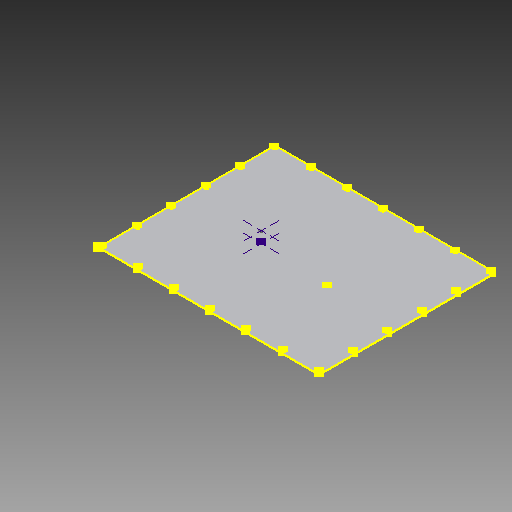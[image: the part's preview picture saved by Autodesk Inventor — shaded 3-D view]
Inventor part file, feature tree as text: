
AUTODESK INVENTOR PART (.ipt)
format: ipt  version: 2017 (Build 210142000, 142)  size: 188,416 bytes
history: native  units: in
note: dims shown in document units (in); Inventor stores cm internally (conversion verified against a paired STEP export)
features: sketch x5, hole x4, pattern_linear x4, extrude x1
ambient origin geometry x8: Origin, YZ Plane, XZ Plane, XY Plane, X Axis, Y Axis, Z Axis, Center Point
bodies: Solid1 (feature_tree)
feature tree (14):
  extrude  "Extrusion1"  Depth=8.0in
  sketch  "Sketch2"  dims[d4=0.06in d5=0.0in]
  hole  "Hole1"  [1 undecoded]
  pattern_linear  "Rectangular Pattern1"  Count1=7 Spacing1=1.635in
  pattern_linear  "Rectangular Pattern2"  Count1=5 Spacing1=1.562in
  hole  "Hole2"  [1 undecoded]
  pattern_linear  "Rectangular Pattern3"  Count1=5 Spacing1=1.562in
  pattern_linear  "Rectangular Pattern4"  Count1=7 Spacing1=1.635in
  sketch  "Sketch3"  dims[d6=0.096in d7=0.75in d8=0.16in d9=0.25in d10=0.5635in d11=1.0in d12=0.8108in d13=0.0935in]
  sketch  "Sketch6"  dims[d14=0.0935in d15=2.7559in d17=1.635in d18=1.9685in d20=1.562in]
  sketch  "Sketch7"  dims[d21=0.0935in d22=0.0935in d23=0.096in d24=0.75in d25=0.16in d26=0.25in d27=0.5635in d28=1.0in d29=0.8108in d30=1.9685in d32=1.562in d33=2.7559in d35=1.635in d36=0.128in d37=0.75in d38=0.232in d39=0.25in d40=0.5635in d41=0.06in d42=0.8108in d43=0.128in d44=0.75in d45=0.232in d46=0.25in d47=0.5635in d48=1.0in d49=0.8108in d50=4.344in d51=3.844in d52=3.062in d53=3.562in]
  hole  "Hole3"  [1 undecoded]
  hole  "Hole4"  [1 undecoded]
  sketch  "Sketch1"  dims[d0=10.0in d3=8.0in]
note: 4 required parameter values undecoded (feature->parameter linkage not recoverable at this tier; creation-order binding heuristic only, values carry confidence <= 0.55)
